FCSTD DOCUMENT  (FreeCAD 0.20R29603 (Git))
Label: plywood_frame
License: All rights reserved
LicenseURL: http://en.wikipedia.org/wiki/All_rights_reserved
objects: Sketcher::SketchObject×1, PartDesign::Body×1
note: 2 computed .brp shape members not serialized (recipe doc carries the construction recipe); baked Part::Feature solids carry a one-line shape summary decoded from their .brp

FEATURE [Sketcher::SketchObject] Sketch
  FullyConstrained = false
  MapMode = 5
  Support = -> [XY_Plane]
  sketch-geometry (12):
    g0: LineSegment StartX=-145 StartY=145 StartZ=0 EndX=145 EndY=145 EndZ=0
    g1: LineSegment StartX=145 StartY=145 StartZ=0 EndX=145 EndY=-145 EndZ=0
    g2: LineSegment StartX=145 StartY=-145 StartZ=0 EndX=-145 EndY=-145 EndZ=0
    g3: LineSegment StartX=-145 StartY=-145 StartZ=0 EndX=-145 EndY=145 EndZ=0
    g4: ArcOfCircle CenterX=-145 CenterY=145 CenterZ=0 NormalX=0 NormalY=0 NormalZ=1 AngleXU=0 Radius=11.6869 StartAngle=2.11541 EndAngle=3.19227
    g5: ArcOfCircle CenterX=145 CenterY=145 CenterZ=0 NormalX=0 NormalY=0 NormalZ=1 AngleXU=0 Radius=10 StartAngle=6.28028 EndAngle=7.82621
    g6: ArcOfCircle CenterX=145 CenterY=-145 CenterZ=0 NormalX=0 NormalY=0 NormalZ=1 AngleXU=0 Radius=13.5638 StartAngle=4.75065 EndAngle=7.02499
    g7: ArcOfCircle CenterX=-145 CenterY=-145 CenterZ=0 NormalX=0 NormalY=0 NormalZ=1 AngleXU=0 Radius=14.3602 StartAngle=2.51974 EndAngle=5.04908
    g8: LineSegment StartX=-140.256 StartY=-158.554 StartZ=0 EndX=145.519 EndY=-158.554 EndZ=0
    g9: LineSegment StartX=155 StartY=-135.836 StartZ=0 EndX=155 EndY=144.971 EndZ=0
    g10: LineSegment StartX=-156.672 StartY=-136.635 StartZ=0 EndX=-156.672 EndY=144.408 EndZ=0
    g11: LineSegment StartX=-151.055 StartY=154.996 StartZ=0 EndX=145.278 EndY=154.996 EndZ=0
  constraints (28):
    c: Coincident(g0,g1)
    c: Coincident(g1,g2)
    c: Coincident(g2,g3)
    c: Coincident(g3,g0)
    c: Horizontal(g0)
    c: Horizontal(g2)
    c: Vertical(g1)
    c: Vertical(g3)
    c: Symmetric(g0,g2,g-1)
    c: DistanceX(g0,g0) = 290
    c: DistanceY(g1,g1) = 290
    c: Coincident(g4,g0)
    c: Coincident(g5,g0)
    c: Coincident(g6,g1)
    c: Coincident(g7,g2)
    c: Coincident(g8,g7)
    c: Coincident(g8,g6)
    c: Horizontal(g8)
    c: Coincident(g9,g6)
    c: Vertical(g9)
    c: Coincident(g5,g9)
    c: Coincident(g10,g7)
    c: Coincident(g10,g4)
    c: Vertical(g10)
    c: Coincident(g11,g4)
    c: Coincident(g11,g5)
    c: Horizontal(g11)
    c: Diameter(g5) = 20
FEATURE [PartDesign::Body] Body
  Group = -> [Sketch]
  Origin = -> Origin
